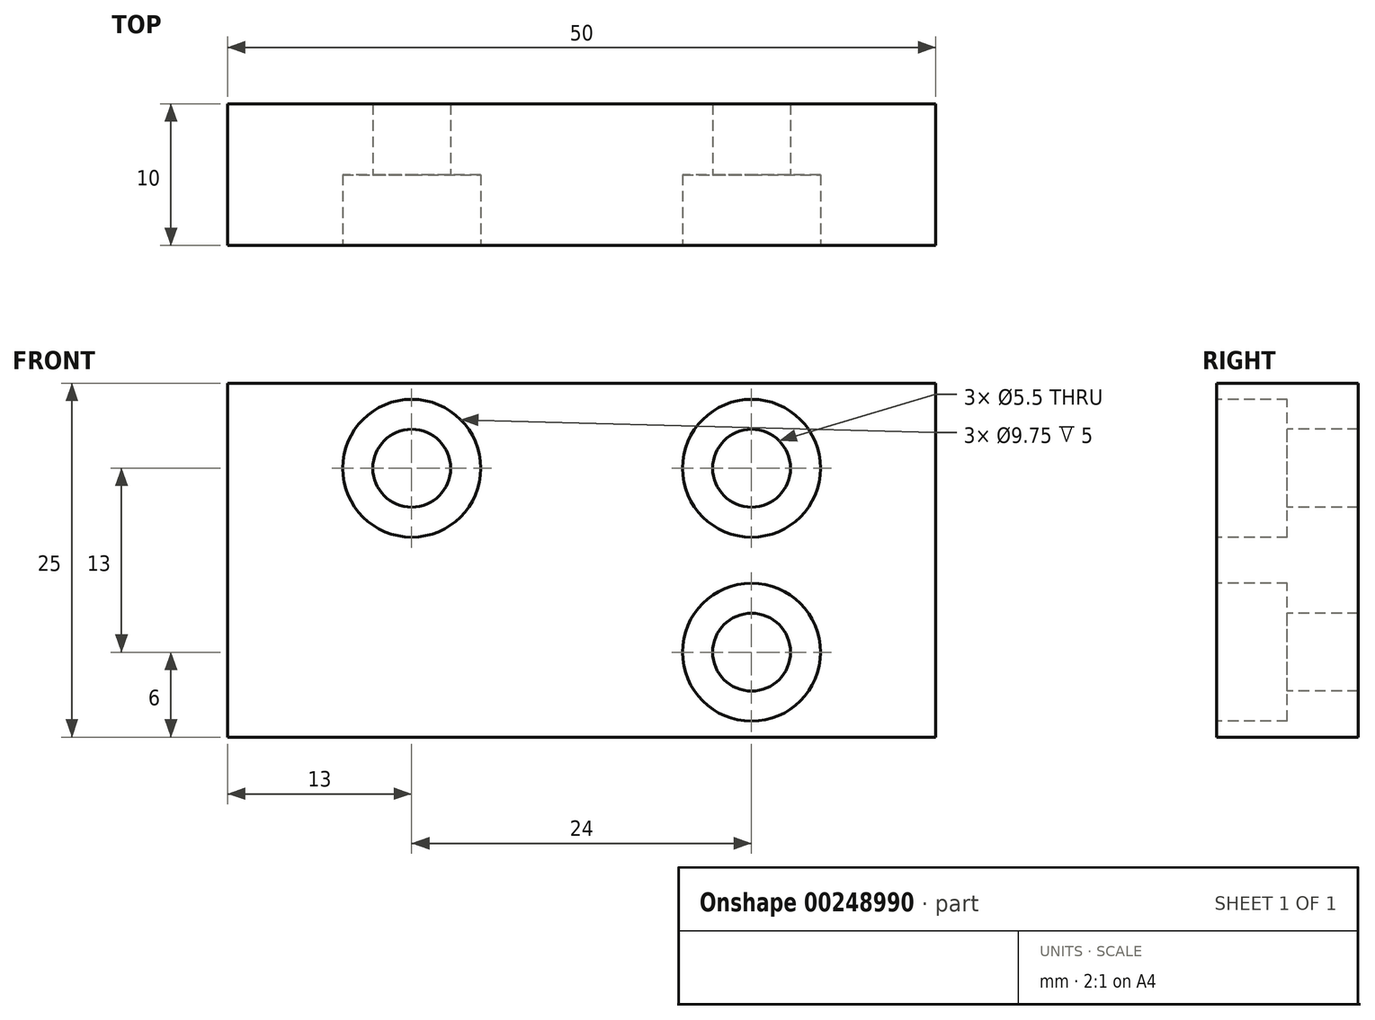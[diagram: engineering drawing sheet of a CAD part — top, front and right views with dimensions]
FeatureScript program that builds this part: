
annotation { "Feature Type Name" : "Feature", "Feature Type Description" : "" }
export const myFeature = defineFeature(function(context is Context, id is Id, definition is map)
    precondition{}
    {
        {
            var Q0;
            Q0=qCreatedBy(makeId("Front.planeOp"),FACE);
            var sketch = newSketch(context, id + "F0", { "sketchPlane" : qUnion([Q0])});
            skLineSegment(sketch, "E0.bottom", {"start": v(25, -12.5) * mm, "end": v(-25, -12.5) * mm});
            skLineSegment(sketch, "E0.top", {"start": v(25, 12.5) * mm, "end": v(-25, 12.5) * mm});
            skLineSegment(sketch, "E0.left", {"start": v(25, -12.5) * mm, "end": v(25, 12.5) * mm});
            skLineSegment(sketch, "E0.right", {"start": v(-25, -12.5) * mm, "end": v(-25, 12.5) * mm});
            skPoint(sketch, "E0.middle", {"position": v(0, 0) * mm});
            skPoint(sketch, "E1", {"position": v(-12, 6.5) * mm});
            skPoint(sketch, "E2", {"position": v(12, 6.5) * mm});
            skPoint(sketch, "E3", {"position": v(12, -6.5) * mm});
            skSolve(sketch);
        }
        {
            var Q0;
            Q0=makeQuery(id+"F0.imprint","IMPRINT",FACE,{"disambiguationData":[TD([[makeQuery(id+"F0.imprint","IMPRINT",EDGE,{"derivedFrom":sQuery(id+"F0.wireOp",EDGE,"E0.bottom")}),-1.0]])]});
            extrude(context, id + "F1", {"entities" : qUnion([Q0]), "oppositeDirection" : true, "depth" : 10 * mm});
        }
        {
            var Q0;
            Q0=sQuery(id+"F0.wireOp",VERTEX,"E1");
            var Q1;
            Q1=sQuery(id+"F0.wireOp",VERTEX,"E2");
            var Q2;
            Q2=sQuery(id+"F0.wireOp",VERTEX,"E3");
            var Q3;
            Q3=makeQuery(id+"F1.opExtrude","SWEPT_BODY",BODY,{"disambiguationData":[OSD([sQuery(id+"F0.wireOp",EDGE,"E0.bottom"),sQuery(id+"F0.wireOp",EDGE,"E0.top"),sQuery(id+"F0.wireOp",EDGE,"E0.left"),sQuery(id+"F0.wireOp",EDGE,"E0.right")])]});
            hole(context, id + "F2", {"style" : HoleStyle.C_BORE, "endStyle" : HoleEndStyle.BLIND, "standardTappedOrClearance" : lookupTablePath({ "standard" : "ISO", "fit" : "Normal", "size" : "M5", "type" : "Clearance" }), "standardBlindInLast" : lookupTablePath({ "fit" : "Standard", "standard" : "ISO", "size" : "M5", "type" : "Clearance" }), "holeDiameter" : 5.5 * mm, "cBoreDiameter" : 9.75 * mm, "cBoreDepth" : 5 * mm, "holeDepth" : 14 * mm, "tappedDepth" : 11.6 * mm, "tapClearance" : 3, "startFromSketch" : true, "locations" : qUnion([Q0, Q1, Q2]), "scope" : qUnion([Q3])});
        }
    });
